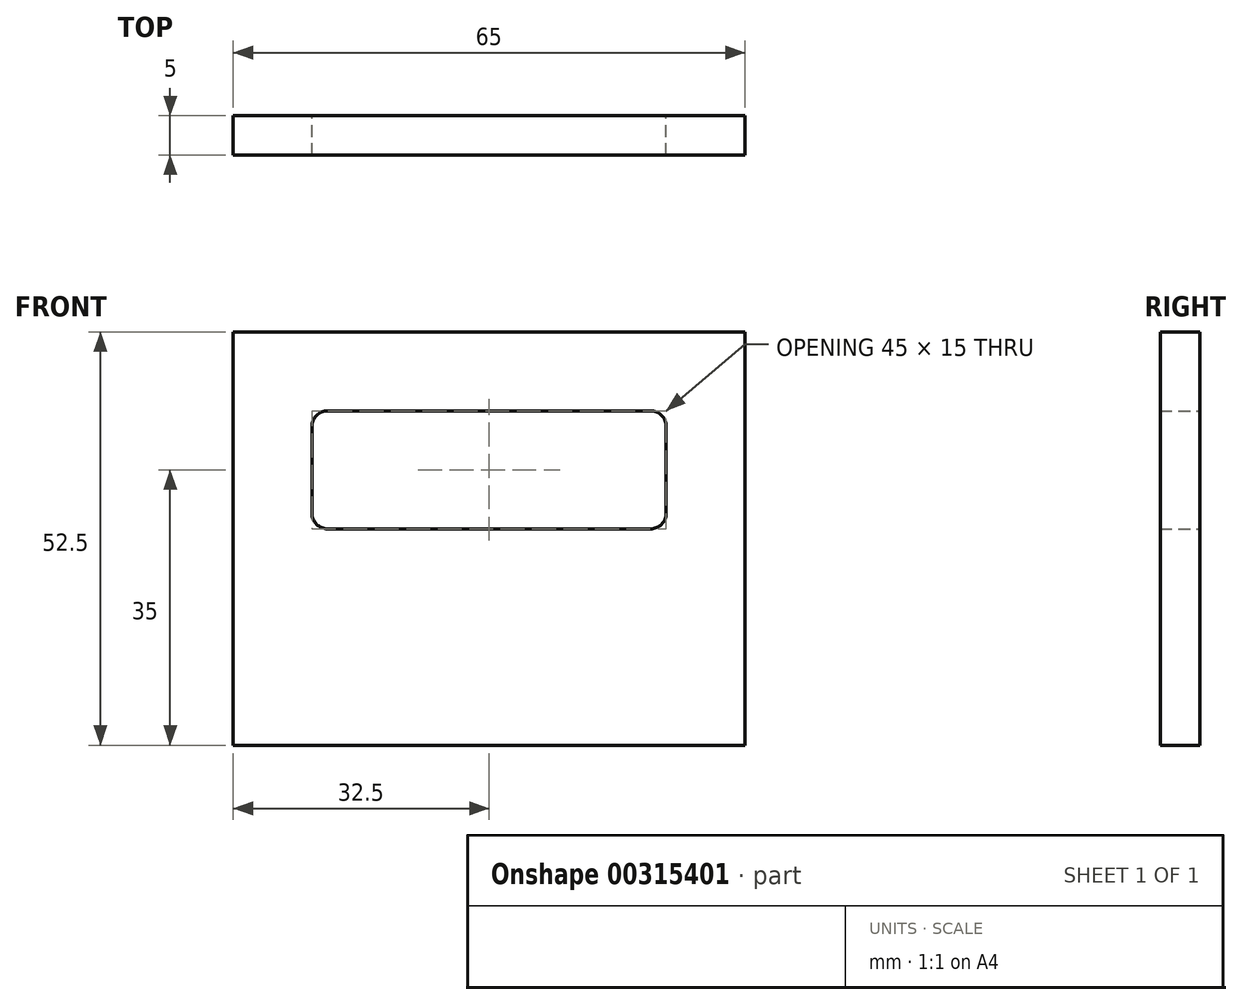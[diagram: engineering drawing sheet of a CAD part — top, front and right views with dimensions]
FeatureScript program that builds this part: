
annotation { "Feature Type Name" : "Feature", "Feature Type Description" : "" }
export const myFeature = defineFeature(function(context is Context, id is Id, definition is map)
    precondition{}
    {
        {
            var Q0;
            Q0=qCreatedBy(makeId("Front.planeOp"),FACE);
            var sketch = newSketch(context, id + "F0", { "sketchPlane" : qUnion([Q0])});
            skLineSegment(sketch, "E0.bottom", {"start": v(-32.5, 26.25) * mm, "end": v(32.5, 26.25) * mm});
            skLineSegment(sketch, "E0.top", {"start": v(-32.5, -26.25) * mm, "end": v(32.5, -26.25) * mm});
            skLineSegment(sketch, "E0.left", {"start": v(-32.5, 26.25) * mm, "end": v(-32.5, -26.25) * mm});
            skLineSegment(sketch, "E0.right", {"start": v(32.5, 26.25) * mm, "end": v(32.5, -26.25) * mm});
            skPoint(sketch, "E0.middle", {"position": v(0, 0) * mm});
            skLineSegment(sketch, "E1.bottom", {"start": v(-20.5, 16.25) * mm, "end": v(20.5, 16.25) * mm});
            skLineSegment(sketch, "E1.top", {"start": v(-20.5, 1.25) * mm, "end": v(20.5, 1.25) * mm});
            skLineSegment(sketch, "E1.left", {"start": v(-22.5, 14.25) * mm, "end": v(-22.5, 3.25) * mm});
            skLineSegment(sketch, "E1.right", {"start": v(22.5, 14.25) * mm, "end": v(22.5, 3.25) * mm});
            skPoint(sketch, "E1.middle", {"position": v(0, 8.75) * mm});
            skPoint(sketch, "E2.visualSharp", {"position": v(-22.5, 16.25) * mm});
            skArc(sketch, "E2.filletArc", {"start": v(-20.5, 16.25) * mm, "mid": v(-21.91, 15.66) * mm, "end": v(-22.5, 14.25) * mm});
            skPoint(sketch, "E3.visualSharp", {"position": v(-22.5, 1.25) * mm});
            skArc(sketch, "E3.filletArc", {"start": v(-22.5, 3.25) * mm, "mid": v(-21.91, 1.84) * mm, "end": v(-20.5, 1.25) * mm});
            skPoint(sketch, "E4.visualSharp", {"position": v(22.5, 1.25) * mm});
            skArc(sketch, "E4.filletArc", {"start": v(20.5, 1.25) * mm, "mid": v(21.91, 1.84) * mm, "end": v(22.5, 3.25) * mm});
            skPoint(sketch, "E5.visualSharp", {"position": v(22.5, 16.25) * mm});
            skArc(sketch, "E5.filletArc", {"start": v(22.5, 14.25) * mm, "mid": v(21.91, 15.66) * mm, "end": v(20.5, 16.25) * mm});
            skSolve(sketch);
        }
        {
            var Q0;
            Q0=makeQuery(id+"F0.imprint","IMPRINT",FACE,{"disambiguationData":[TD([[makeQuery(id+"F0.imprint","IMPRINT",EDGE,{"derivedFrom":sQuery(id+"F0.wireOp",EDGE,"E0.bottom")}),-1.0]])]});
            extrude(context, id + "F1", {"entities" : qUnion([Q0]), "depth" : 5 * mm});
        }
    });
